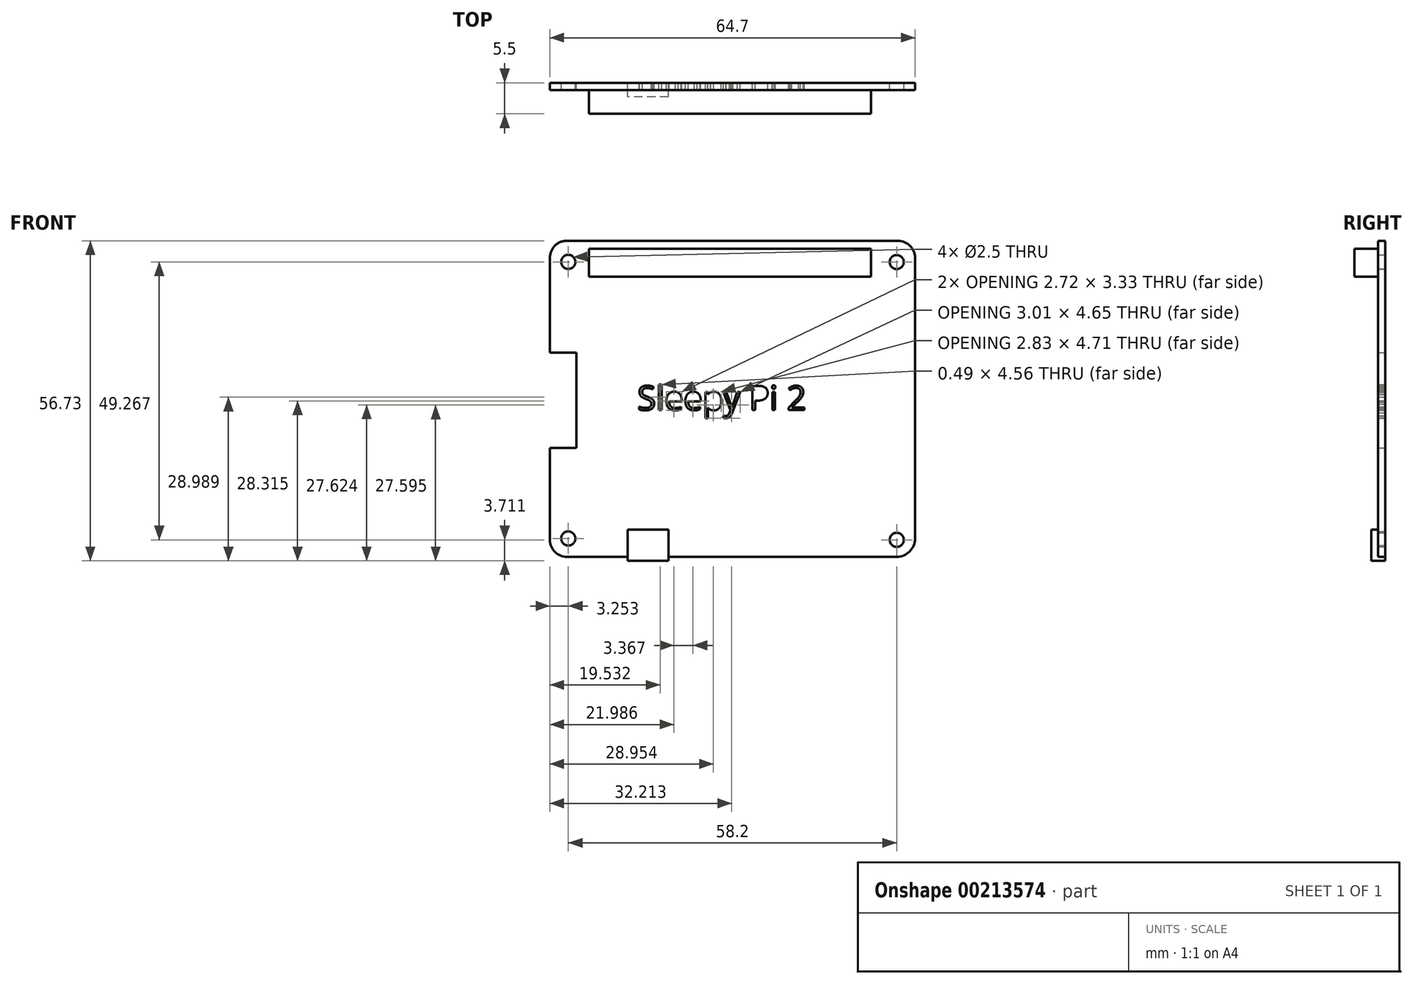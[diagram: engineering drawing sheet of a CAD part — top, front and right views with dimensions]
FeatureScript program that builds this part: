
annotation { "Feature Type Name" : "Feature", "Feature Type Description" : "" }
export const myFeature = defineFeature(function(context is Context, id is Id, definition is map)
    precondition{}
    {
        {
            var Q0;
            Q0=qCreatedBy(makeId("Front.planeOp"),FACE);
            var sketch = newSketch(context, id + "F0", { "sketchPlane" : qUnion([Q0])});
            skLineSegment(sketch, "E0", {"start": v(36.21, 20.56) * mm, "end": v(36.21, -29.2) * mm});
            skLineSegment(sketch, "E1", {"start": v(32.96, -32.44) * mm, "end": v(-25.49, -32.44) * mm});
            skLineSegment(sketch, "E2", {"start": v(-28.49, -29.44) * mm, "end": v(-28.49, -13.14) * mm});
            skLineSegment(sketch, "E3", {"start": v(-28.49, -13.14) * mm, "end": v(-23.79, -13.14) * mm});
            skLineSegment(sketch, "E4", {"start": v(-23.79, -13.14) * mm, "end": v(-23.79, 3.76) * mm});
            skLineSegment(sketch, "E5", {"start": v(-23.79, 3.76) * mm, "end": v(-28.49, 3.76) * mm});
            skLineSegment(sketch, "E6", {"start": v(-28.49, 3.76) * mm, "end": v(-28.49, 20.59) * mm});
            skLineSegment(sketch, "E7", {"start": v(33.21, 23.56) * mm, "end": v(-25.49, 23.59) * mm});
            skLineSegment(sketch, "E8", {"start": v(36.21, 23.56) * mm, "end": v(36.21, 19.8) * mm, "construction": true});
            skPoint(sketch, "E9.visualSharp", {"position": v(-28.49, 23.59) * mm});
            skArc(sketch, "E9.filletArc", {"start": v(-25.49, 23.59) * mm, "mid": v(-27.6, 22.7) * mm, "end": v(-28.49, 20.59) * mm});
            skPoint(sketch, "E10.visualSharp", {"position": v(-28.49, -32.44) * mm});
            skArc(sketch, "E10.filletArc", {"start": v(-28.49, -29.44) * mm, "mid": v(-27.6, -31.56) * mm, "end": v(-25.49, -32.44) * mm});
            skPoint(sketch, "E11.visualSharp", {"position": v(36.21, -32.44) * mm});
            skArc(sketch, "E11.filletArc", {"start": v(32.96, -32.44) * mm, "mid": v(35.26, -31.5) * mm, "end": v(36.21, -29.2) * mm});
            skPoint(sketch, "E12.visualSharp", {"position": v(36.21, 23.56) * mm});
            skArc(sketch, "E12.filletArc", {"start": v(36.21, 20.56) * mm, "mid": v(35.34, 22.68) * mm, "end": v(33.21, 23.56) * mm});
            skLineSegment(sketch, "E13", {"start": v(36.21, 19.8) * mm, "end": v(32.96, 19.8) * mm});
            skCircle(sketch, "E14", {"center": v(32.96, 19.8) * mm, "radius": 1.25 * mm});
            skLineSegment(sketch, "E15", {"start": v(36.21, -32.44) * mm, "end": v(36.21, -29.2) * mm, "construction": true});
            skLineSegment(sketch, "E16", {"start": v(32.96, 19.8) * mm, "end": v(32.96, -46.28) * mm, "construction": true});
            skLineSegment(sketch, "E17", {"start": v(36.21, -29.2) * mm, "end": v(32.96, -29.2) * mm, "construction": true});
            skLineSegment(sketch, "E18", {"start": v(-28.49, -32.44) * mm, "end": v(-25.24, -32.44) * mm, "construction": true});
            skLineSegment(sketch, "E19", {"start": v(-17.6, 23.58) * mm, "end": v(-17.6, 17.18) * mm, "construction": true});
            skLineSegment(sketch, "E20", {"start": v(-28.49, 17.18) * mm, "end": v(-21.59, 17.18) * mm, "construction": true});
            skLineSegment(sketch, "E21", {"start": v(-21.59, 17.18) * mm, "end": v(-21.59, 22.18) * mm});
            skLineSegment(sketch, "E22", {"start": v(-21.59, 17.18) * mm, "end": v(28.41, 17.18) * mm});
            skLineSegment(sketch, "E23", {"start": v(28.41, 17.18) * mm, "end": v(28.41, 22.18) * mm});
            skLineSegment(sketch, "E24", {"start": v(-21.59, 22.18) * mm, "end": v(28.41, 22.18) * mm});
            skCircle(sketch, "E25", {"center": v(32.96, -29.43) * mm, "radius": 1.25 * mm});
            skCircle(sketch, "E26", {"center": v(-25.24, -29.2) * mm, "radius": 1.25 * mm});
            skLineSegment(sketch, "E27", {"start": v(-25.49, 23.59) * mm, "end": v(-25.49, 19.84) * mm, "construction": true});
            skLineSegment(sketch, "E28", {"start": v(-25.24, -32.44) * mm, "end": v(-25.24, 26.6) * mm, "construction": true});
            skLineSegment(sketch, "E29", {"start": v(-25.49, 19.84) * mm, "end": v(-24.6, 19.84) * mm, "construction": true});
            skCircle(sketch, "E30", {"center": v(-25.24, 19.84) * mm, "radius": 1.25 * mm});
            skLineSegment(sketch, "E31", {"start": v(-21.62, -32.44) * mm, "end": v(-21.62, -27.64) * mm, "construction": true});
            skLineSegment(sketch, "E32", {"start": v(-28.49, -27.64) * mm, "end": v(-7.49, -27.64) * mm, "construction": true});
            skLineSegment(sketch, "E33", {"start": v(-21.62, -32.44) * mm, "end": v(-21.62, -33.14) * mm, "construction": true});
            skLineSegment(sketch, "E34", {"start": v(-7.49, -27.64) * mm, "end": v(-7.49, -33.14) * mm});
            skLineSegment(sketch, "E35", {"start": v(-7.49, -33.14) * mm, "end": v(-14.69, -33.14) * mm});
            skLineSegment(sketch, "E36", {"start": v(-14.69, -33.14) * mm, "end": v(-14.69, -27.64) * mm});
            skLineSegment(sketch, "E37", {"start": v(-14.69, -27.64) * mm, "end": v(-7.49, -27.64) * mm});
            skText(sketch, "E38", { "text": "Sleepy Pi 2", "fontName": "OpenSans-Regular.ttf"});
            const initialGuessF0  = {"E38": [-0.01301, -0.00643, 1, 0, 0.00432]};
            skSetInitialGuess(sketch, initialGuessF0);
            skSolve(sketch);
        }
        {
            var Q0;
            Q0=makeQuery(id+"F0.imprint","IMPRINT",FACE,{"disambiguationData":[TD([[makeQuery(id+"F0.imprint","IMPRINT",EDGE,{"derivedFrom":sQuery(id+"F0.wireOp",EDGE,"E21")}),-1.0]])]});
            extrude(context, id + "F1", {"entities" : qUnion([Q0]), "depth" : 5.5 * mm});
        }
        {
            var Q0;
            Q0 = qSketchRegion(id + "F0", true);
            extrude(context, id + "F2", {"entities" : qUnion([Q0]), "operationType" : NewBodyOperationType.ADD, "depth" : 1.3 * mm});
        }
        {
            var Q0;
            {var subQ5=sQuery(id+"F0.wireOp",EDGE,"E37");Q0=makeQuery(id+"F0.imprint","IMPRINT",FACE,{"disambiguationData":[TD([[makeQuery(id+"F0.imprint","IMPRINT",EDGE,{"derivedFrom":subQ5}),-1.0]])]});}
            var Q1;
            {var subQ5=sQuery(id+"F0.wireOp",EDGE,"E35");Q1=makeQuery(id+"F0.imprint","IMPRINT",FACE,{"disambiguationData":[TD([[makeQuery(id+"F0.imprint","IMPRINT",EDGE,{"derivedFrom":subQ5}),-1.0]])]});}
            extrude(context, id + "F3", {"entities" : qUnion([Q0, Q1]), "operationType" : NewBodyOperationType.ADD, "depth" : 2.5 * mm});
        }
    });
